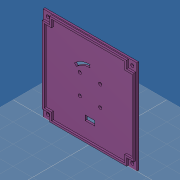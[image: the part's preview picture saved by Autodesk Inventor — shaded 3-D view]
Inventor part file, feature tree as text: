
AUTODESK INVENTOR PART (.ipt)
format: ipt  version: 2019 (Build 230136000, 136)  size: 185,856 bytes
history: native  units: mm
features: extrude x3, sketch x2, hole x1
ambient origin geometry x8: Origin, YZ Plane, XZ Plane, XY Plane, X Axis, Y Axis, Z Axis, Center Point
bodies: Volumenkörper1 (feature_tree)
feature tree (6):
  sketch  "Skizze1"  dims[d0=97.6mm d1=97.6mm]
  extrude  "Extrusion1"  Depth=97.6mm
  hole  "Bohrung1"  [1 undecoded]
  extrude  "Extrusion4"  Depth=5.0mm
  extrude  "Extrusion5"  Depth=10.0mm
  sketch  "Skizze2"  dims[d3=2.0mm d4=0.0mm d20=3.4mm d21=6.0mm d22=4.0mm d23=2.0mm d24=90.0deg d25=8.0mm d26=20.594885mm d27=100.0mm d28=100.0mm d29=10.0mm d30=4.0mm d40=95.5mm d41=2.0mm d42=2.0mm d43=2.0mm d44=0.0mm d45=100.0mm d46=100.0mm d47=40.0mm d51=4.0mm d52=0.0mm d53=3.0mm d54=45.0deg d55=30.0mm d57=10.0mm d58=5.0mm d59=25.0mm]
note: 1 required parameter value undecoded (feature->parameter linkage not recoverable at this tier; creation-order binding heuristic only, values carry confidence <= 0.55)
